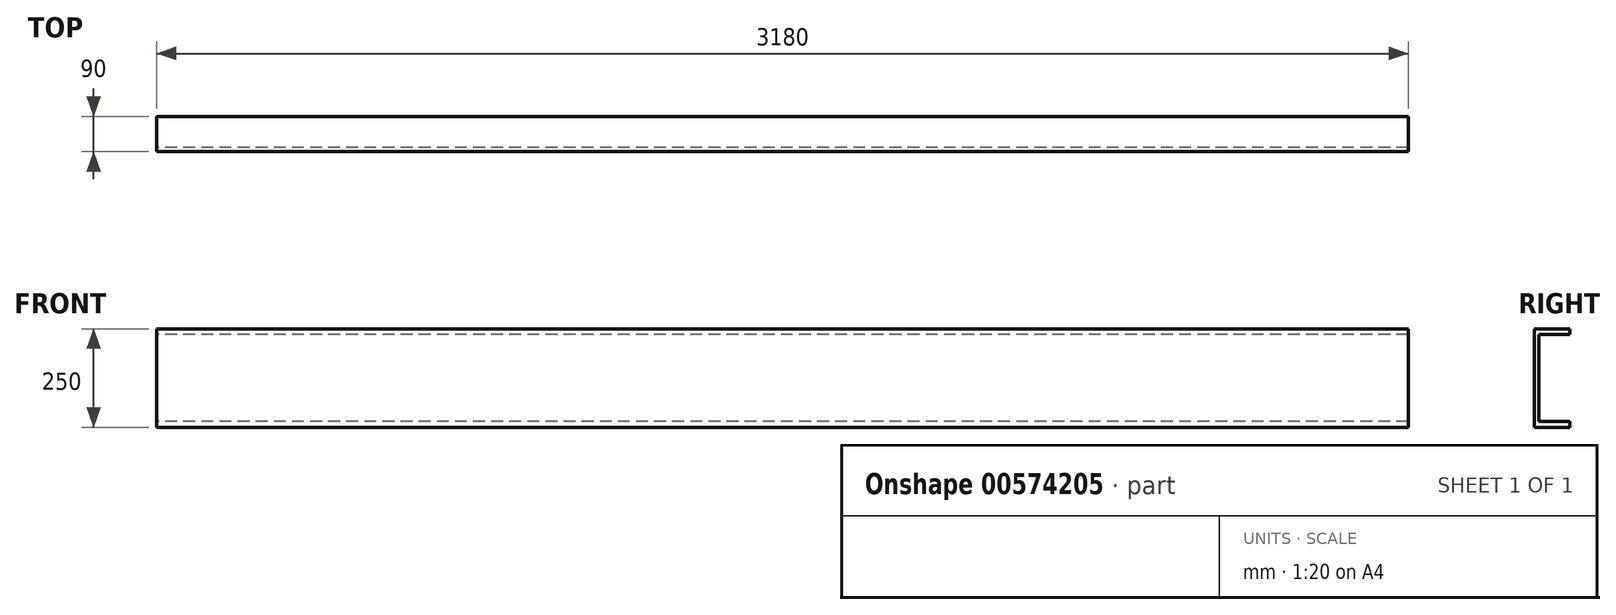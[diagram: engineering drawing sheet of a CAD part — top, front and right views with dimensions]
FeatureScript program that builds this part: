
annotation { "Feature Type Name" : "Feature", "Feature Type Description" : "" }
export const myFeature = defineFeature(function(context is Context, id is Id, definition is map)
    precondition{}
    {
        {
            var Q0;
            Q0=qCreatedBy(makeId("Right.planeOp"),FACE);
            var sketch = newSketch(context, id + "F0", { "sketchPlane" : qUnion([Q0])});
            skLineSegment(sketch, "E0", {"start": v(0, 0) * mm, "end": v(0, 250) * mm});
            skLineSegment(sketch, "E1", {"start": v(0, 250) * mm, "end": v(90, 250) * mm});
            skLineSegment(sketch, "E2", {"start": v(90, 250) * mm, "end": v(90, 235.5) * mm});
            skLineSegment(sketch, "E3", {"start": v(90, 235.5) * mm, "end": v(11, 235.5) * mm});
            skLineSegment(sketch, "E4", {"start": v(11, 235.5) * mm, "end": v(11, 14.5) * mm});
            skLineSegment(sketch, "E5", {"start": v(11, 14.5) * mm, "end": v(90, 14.5) * mm});
            skLineSegment(sketch, "E6", {"start": v(90, 14.5) * mm, "end": v(90, 0) * mm});
            skLineSegment(sketch, "E7", {"start": v(90, 0) * mm, "end": v(0, 0) * mm});
            skSolve(sketch);
        }
        {
            var Q0;
            Q0 = qSketchRegion(id + "F0", true);
            extrude(context, id + "F1", {"entities" : qUnion([Q0]), "depth" : 3180 * mm, "offsetDistance" : 25 * mm});
        }
    });
